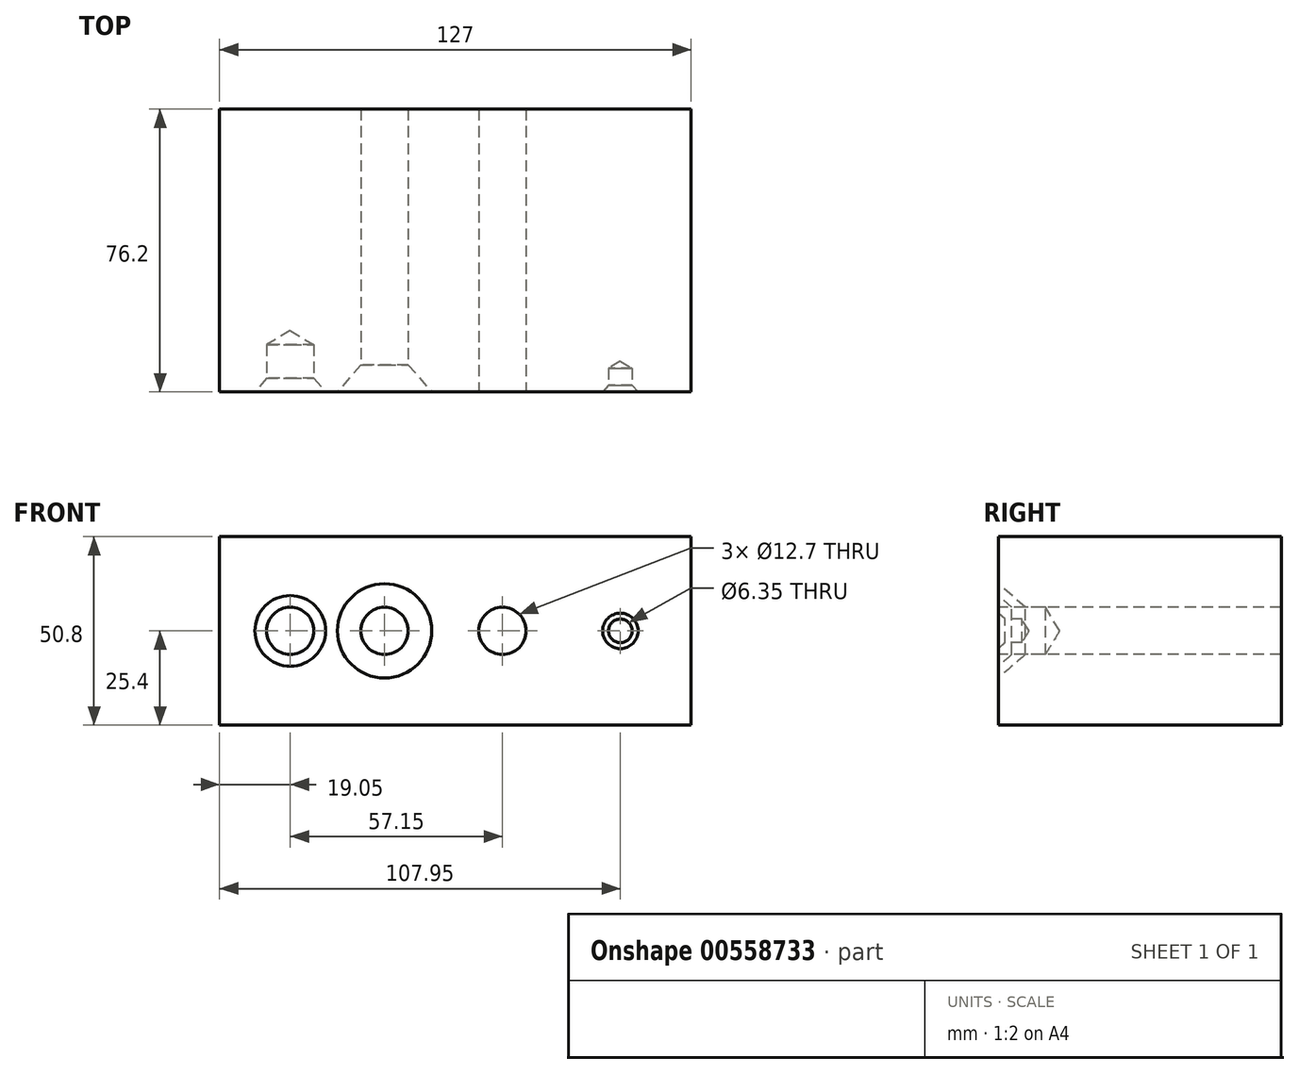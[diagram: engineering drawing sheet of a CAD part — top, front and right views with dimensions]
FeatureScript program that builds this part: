
annotation { "Feature Type Name" : "Feature", "Feature Type Description" : "" }
export const myFeature = defineFeature(function(context is Context, id is Id, definition is map)
    precondition{}
    {
        {
            var Q0;
            Q0=qCreatedBy(makeId("Front.planeOp"),FACE);
            var sketch = newSketch(context, id + "F0", { "sketchPlane" : qUnion([Q0])});
            skLineSegment(sketch, "E0", {"start": v(0, 0) * mm, "end": v(-127, 0) * mm});
            skLineSegment(sketch, "E1", {"start": v(-127, 0) * mm, "end": v(-127, 50.8) * mm});
            skLineSegment(sketch, "E2", {"start": v(-127, 50.8) * mm, "end": v(0, 50.8) * mm});
            skLineSegment(sketch, "E3", {"start": v(0, 50.8) * mm, "end": v(0, 0) * mm});
            skSolve(sketch);
        }
        {
            var Q0;
            Q0=makeQuery(id+"F0.imprint","IMPRINT",FACE,{"disambiguationData":[TD([[makeQuery(id+"F0.imprint","IMPRINT",EDGE,{"derivedFrom":sQuery(id+"F0.wireOp",EDGE,"E0")}),-1.0]])]});
            extrude(context, id + "F1", {"entities" : qUnion([Q0]), "depth" : 76.2 * mm, "offsetDistance" : 25.4 * mm});
        }
        {
            var Q0;
            Q0=makeQuery(id+"F1.opExtrude","CAP_FACE",FACE,{"disambiguationData":[OSD([sQuery(id+"F0.wireOp",EDGE,"E0"),sQuery(id+"F0.wireOp",EDGE,"E1"),sQuery(id+"F0.wireOp",EDGE,"E2"),sQuery(id+"F0.wireOp",EDGE,"E3")])],"isStart":false});
            var sketch = newSketch(context, id + "F2", { "sketchPlane" : qUnion([Q0])});
            skLineSegment(sketch, "E4", {"start": v(-127, 25.4) * mm, "end": v(-107.95, 25.4) * mm});
            skLineSegment(sketch, "E5", {"start": v(-107.95, 25.4) * mm, "end": v(-82.55, 25.4) * mm});
            skLineSegment(sketch, "E6", {"start": v(-82.55, 25.4) * mm, "end": v(-50.8, 25.4) * mm});
            skLineSegment(sketch, "E7", {"start": v(-50.8, 25.4) * mm, "end": v(-19.05, 25.4) * mm});
            skPoint(sketch, "E8", {"position": v(-107.95, 25.4) * mm});
            skPoint(sketch, "E9", {"position": v(-82.55, 25.4) * mm});
            skPoint(sketch, "E10", {"position": v(-50.8, 25.4) * mm});
            skPoint(sketch, "E11", {"position": v(-19.05, 25.4) * mm});
            skSolve(sketch);
        }
        {
            var Q0;
            Q0=sQuery(id+"F2.wireOp",VERTEX,"E8");
            var Q1;
            Q1=makeQuery(id+"F1.opExtrude","SWEPT_BODY",BODY,{"disambiguationData":[OSD([sQuery(id+"F0.wireOp",EDGE,"E0"),sQuery(id+"F0.wireOp",EDGE,"E1"),sQuery(id+"F0.wireOp",EDGE,"E2"),sQuery(id+"F0.wireOp",EDGE,"E3")])]});
            hole(context, id + "F3", {"style" : HoleStyle.C_SINK, "endStyle" : HoleEndStyle.BLIND, "holeDiameter" : 12.7 * mm, "cSinkDiameter" : 19.05 * mm, "cSinkAngle" : 82 * degree, "holeDepth" : 12.7 * mm, "isTappedThrough" : true, "tappedDepth" : 12.7 * mm, "tapClearance" : 3, "locations" : qUnion([Q0]), "scope" : qUnion([Q1])});
        }
        {
            var Q0;
            Q0=sQuery(id+"F2.wireOp",VERTEX,"E9");
            var Q1;
            Q1=makeQuery(id+"F1.opExtrude","SWEPT_BODY",BODY,{"disambiguationData":[OSD([sQuery(id+"F0.wireOp",EDGE,"E0"),sQuery(id+"F0.wireOp",EDGE,"E1"),sQuery(id+"F0.wireOp",EDGE,"E2"),sQuery(id+"F0.wireOp",EDGE,"E3")])]});
            hole(context, id + "F4", {"style" : HoleStyle.C_SINK, "endStyle" : HoleEndStyle.THROUGH, "holeDiameter" : 12.7 * mm, "cSinkDiameter" : 25.4 * mm, "cSinkAngle" : 82 * degree, "isTappedThrough" : true, "tappedDepth" : 12.7 * mm, "tapClearance" : 3, "locations" : qUnion([Q0]), "scope" : qUnion([Q1])});
        }
        {
            var Q0;
            Q0=sQuery(id+"F2.wireOp",VERTEX,"E10");
            var Q1;
            Q1=makeQuery(id+"F1.opExtrude","SWEPT_BODY",BODY,{"disambiguationData":[OSD([sQuery(id+"F0.wireOp",EDGE,"E0"),sQuery(id+"F0.wireOp",EDGE,"E1"),sQuery(id+"F0.wireOp",EDGE,"E2"),sQuery(id+"F0.wireOp",EDGE,"E3")])]});
            hole(context, id + "F5", {"style" : HoleStyle.SIMPLE, "endStyle" : HoleEndStyle.THROUGH, "holeDiameter" : 12.7 * mm, "isTappedThrough" : true, "tappedDepth" : 12.7 * mm, "tapClearance" : 3, "locations" : qUnion([Q0]), "scope" : qUnion([Q1])});
        }
        {
            var Q0;
            Q0=sQuery(id+"F2.wireOp",VERTEX,"E11");
            var Q1;
            Q1=makeQuery(id+"F1.opExtrude","SWEPT_BODY",BODY,{"disambiguationData":[OSD([sQuery(id+"F0.wireOp",EDGE,"E0"),sQuery(id+"F0.wireOp",EDGE,"E1"),sQuery(id+"F0.wireOp",EDGE,"E2"),sQuery(id+"F0.wireOp",EDGE,"E3")])]});
            hole(context, id + "F6", {"style" : HoleStyle.C_SINK, "endStyle" : HoleEndStyle.BLIND, "holeDiameter" : 6.35 * mm, "cSinkDiameter" : 9.52 * mm, "cSinkAngle" : 82 * degree, "holeDepth" : 6.35 * mm, "isTappedThrough" : true, "tappedDepth" : 12.7 * mm, "tapClearance" : 3, "locations" : qUnion([Q0]), "scope" : qUnion([Q1])});
        }
    });
